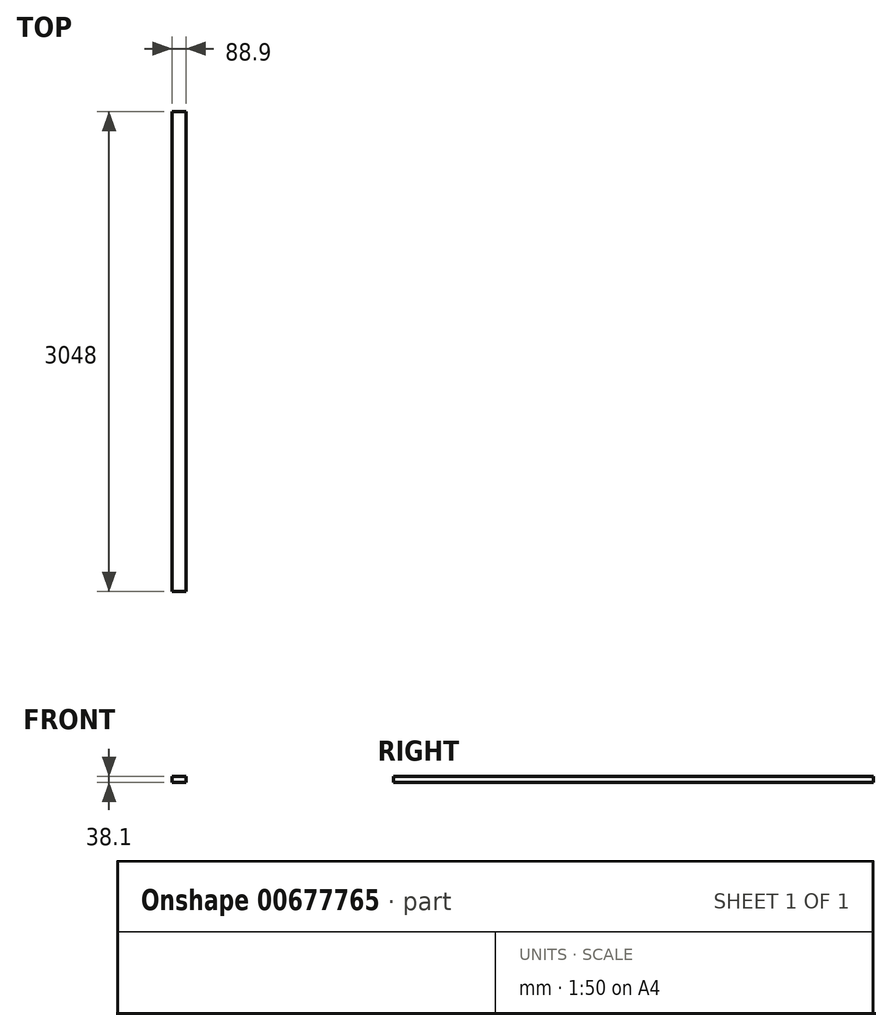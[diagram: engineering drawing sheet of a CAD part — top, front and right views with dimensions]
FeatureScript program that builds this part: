
annotation { "Feature Type Name" : "Feature", "Feature Type Description" : "" }
export const myFeature = defineFeature(function(context is Context, id is Id, definition is map)
    precondition{}
    {
        {
            var Q0;
            Q0=qCreatedBy(makeId("Front.planeOp"),FACE);
            var sketch = newSketch(context, id + "F0", { "sketchPlane" : qUnion([Q0])});
            skLineSegment(sketch, "E0.bottom", {"start": v(1067.64, -126.43) * mm, "end": v(1156.54, -126.43) * mm});
            skLineSegment(sketch, "E0.top", {"start": v(1067.64, -164.53) * mm, "end": v(1156.54, -164.53) * mm});
            skLineSegment(sketch, "E0.left", {"start": v(1067.64, -126.43) * mm, "end": v(1067.64, -164.53) * mm});
            skLineSegment(sketch, "E0.right", {"start": v(1156.54, -126.43) * mm, "end": v(1156.54, -164.53) * mm});
            skSolve(sketch);
        }
        {
            var Q0;
            Q0=makeQuery(id+"F0.imprint","IMPRINT",FACE,{"disambiguationData":[TD([[makeQuery(id+"F0.imprint","IMPRINT",EDGE,{"derivedFrom":sQuery(id+"F0.wireOp",EDGE,"E0.bottom")}),-1.0]])]});
            extrude(context, id + "F1", {"entities" : qUnion([Q0]), "depth" : 3048 * mm, "offsetDistance" : 25.4 * mm});
        }
    });
